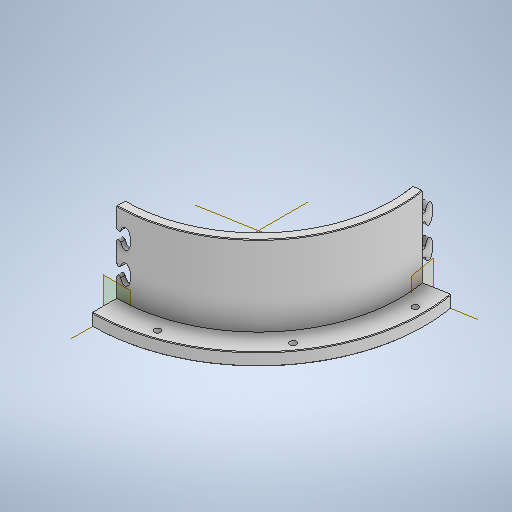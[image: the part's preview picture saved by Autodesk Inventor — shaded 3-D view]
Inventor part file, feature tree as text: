
AUTODESK INVENTOR PART (.ipt)
format: ipt  version: 2025 (Build 290162000, 162)  size: 442,880 bytes
history: native  units: in
note: dims shown in document units (in); Inventor stores cm internally (conversion verified against a paired STEP export)
features: other x16, sketch x7, extrude x7, chamfer x2
ambient origin geometry x8: Origin, YZ Plane, XZ Plane, XY Plane, X Axis, Y Axis, Z Axis, Center Point
bodies: Solid1 (feature_tree)
feature tree (32):
  other  "Table"
  other  "Cylinder Segment - 01"
  other  "Cylinder Segment - 02"
  other  "Cylinder Segment - 03"
  other  "Cylinder Segment - 04"
  other  "Cylinder Segment - 05"
  other  "Cylinder Segment - 06"
  other  "Cylinder Segment - 07"
  other  "Cylinder Segment - 08"
  other  "Cylinder Segment - 09"
  other  "Cylinder Segment - 10"
  other  "Cylinder Segment - Face"
  sketch  "Sketch1"  dims[d5=0.0in d7=0.0in]
  extrude  "Extrusion1"  TaperAngle=0.0deg  [1 undecoded]
  extrude  "Extrusion2"  Depth=0.0787in TaperAngle=45.0deg
  extrude  "Extrusion7"  Depth=10.0394in
  chamfer  "Chamfer1"  Distance=3.937in Angle=360.0deg
  chamfer  "Chamfer2"  Distance=0.3937in
  extrude  "Extrusion8"  TaperAngle=0.0deg  [1 undecoded]
  extrude  "Quadrant Cut"  Depth=0.7874in
  other  "Bf Plane"
  other  "Am Plane"
  extrude  "Extrusion10"  Depth=0.3937in TaperAngle=0.0deg
  extrude  "Extrusion11"  Depth=0.3189in
  sketch  "Sketch2"  dims[d25=0.0787in d26=45.0deg d27=10.0394in]
  sketch  "Sketch3"  dims[d28=0.1969in d29=3.937in d31=360.0deg d33=0.3937in d34=0.0in]
  sketch  "Sketch Circular Pattern1"  dims[d18=0.0in d22=0.0787in d23=45.0deg]
  sketch  "Sketch5"  dims[d48=0.5497in d49=0.0in d50=0.0in]
  other  "Work Axis1"
  other  "Work Axis2"
  sketch  "Sketch6"  dims[d57=0.315in d58=0.1575in d60=0.7874in]
  sketch  "Sketch7"  dims[d61=1.2795in d64=0.3937in d65=0.0in d66=0.1181in d67=0.1772in d68=0.1614in d69=0.3189in d70=0.1772in d71=0.122in d73=0.0039in d74=0.0039in d75=1.2795in d76=0.0in d77=0.0in]
note: 2 required parameter values undecoded (feature->parameter linkage not recoverable at this tier; creation-order binding heuristic only, values carry confidence <= 0.55)
